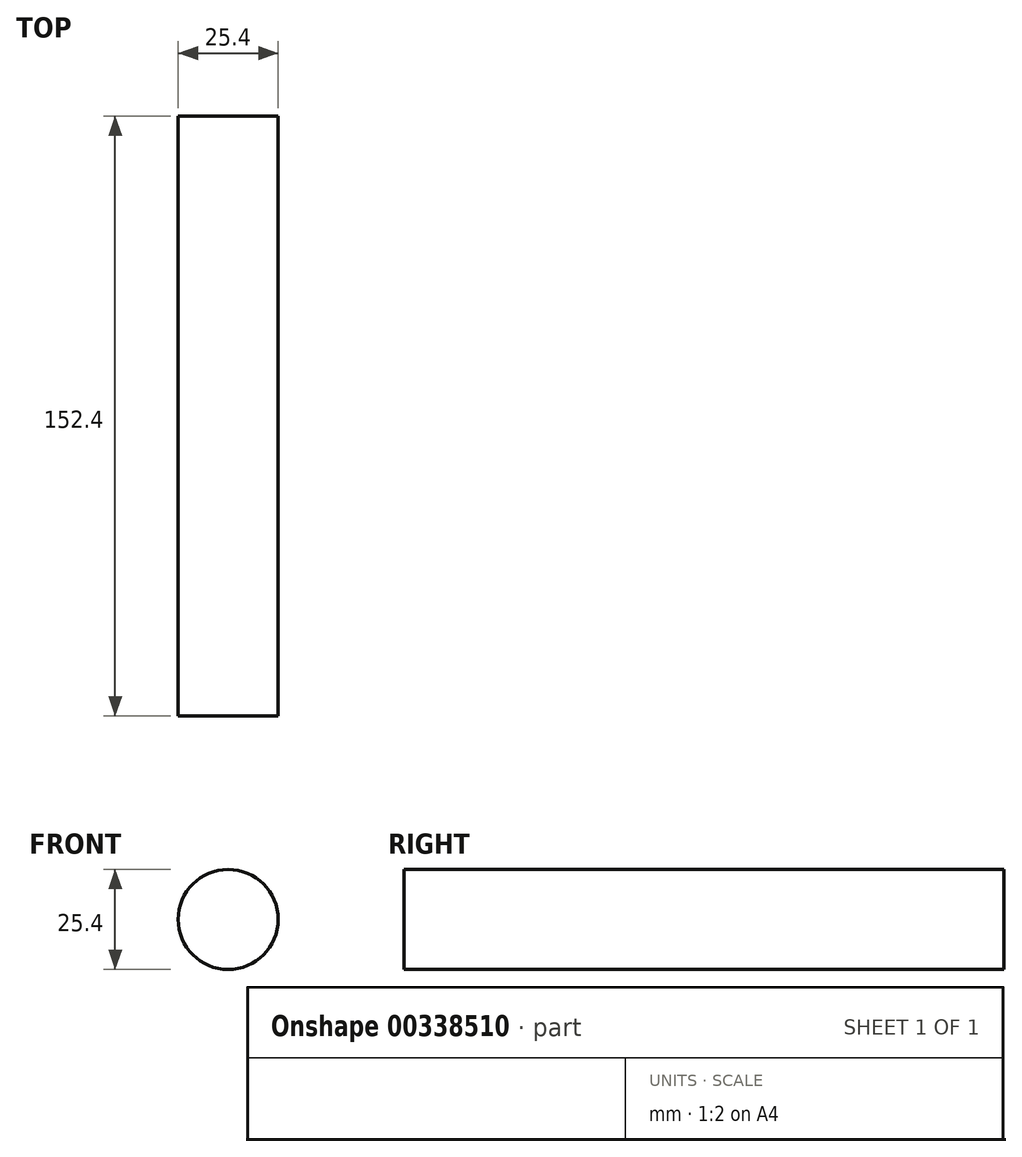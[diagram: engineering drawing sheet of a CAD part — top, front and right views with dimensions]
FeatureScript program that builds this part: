
annotation { "Feature Type Name" : "Feature", "Feature Type Description" : "" }
export const myFeature = defineFeature(function(context is Context, id is Id, definition is map)
    precondition{}
    {
        {
            var Q0;
            Q0=qCreatedBy(makeId("Front.planeOp"),FACE);
            var sketch = newSketch(context, id + "F0", { "sketchPlane" : qUnion([Q0])});
            skCircle(sketch, "E0", {"center": v(0, 0) * mm, "radius": 12.7 * mm});
            skSolve(sketch);
        }
        {
            var Q0;
            Q0=makeQuery(id+"F0.imprint","IMPRINT",FACE,{"disambiguationData":[TD([[makeQuery(id+"F0.imprint","IMPRINT",EDGE,{"derivedFrom":sQuery(id+"F0.wireOp",EDGE,"E0")}),1.0]])]});
            extrude(context, id + "F1", {"entities" : qUnion([Q0]), "depth" : 152.4 * mm});
        }
    });
